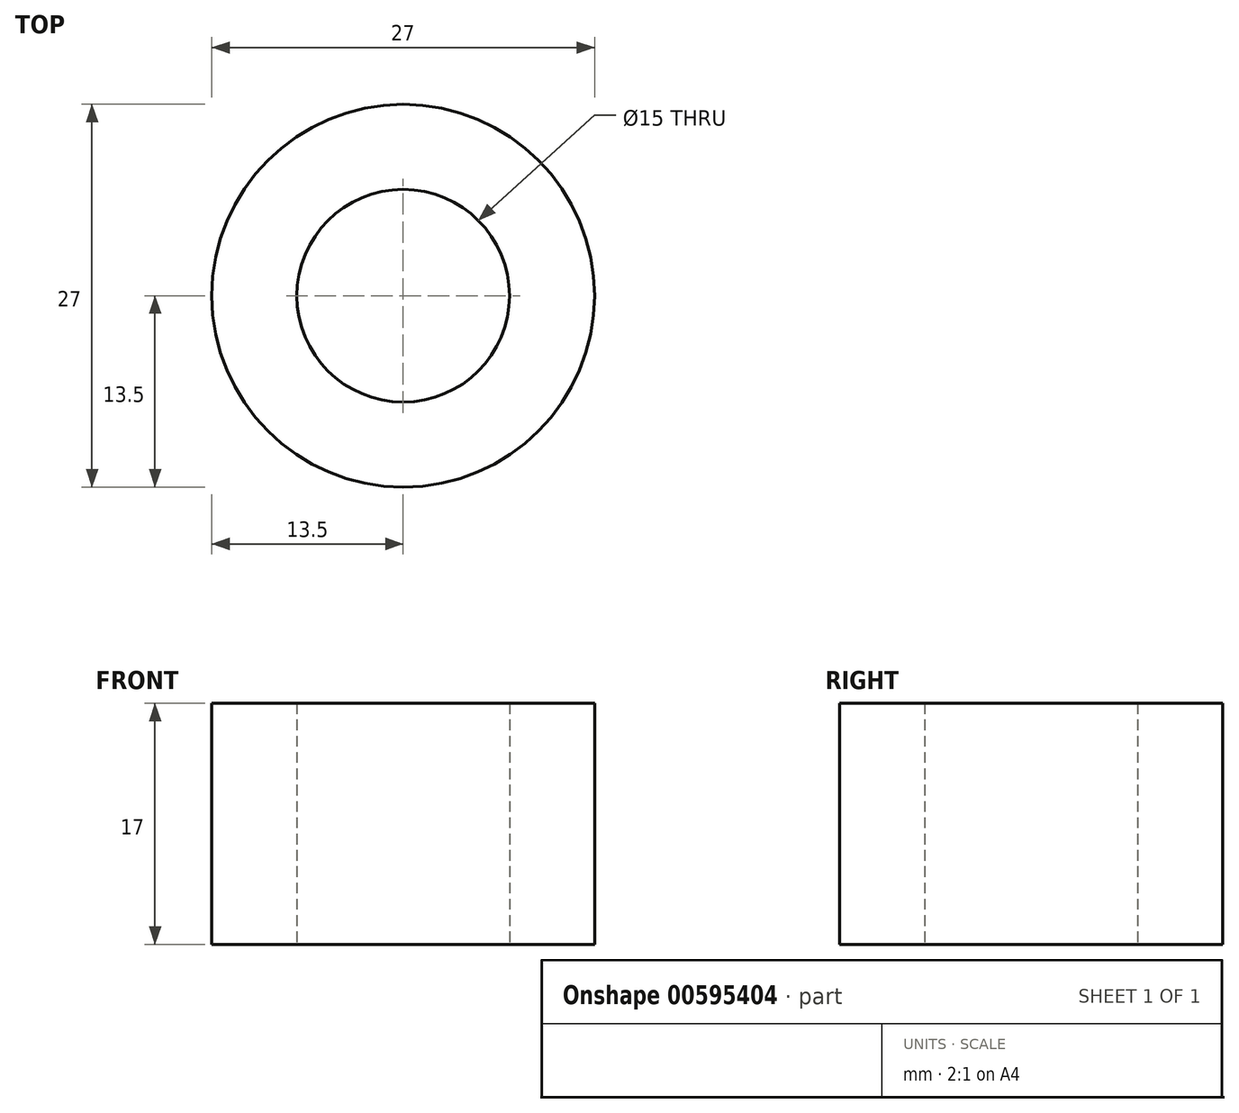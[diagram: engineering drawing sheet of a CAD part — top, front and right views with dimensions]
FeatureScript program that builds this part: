
annotation { "Feature Type Name" : "Feature", "Feature Type Description" : "" }
export const myFeature = defineFeature(function(context is Context, id is Id, definition is map)
    precondition{}
    {
        {
            var Q0;
            Q0=qCreatedBy(makeId("Top.planeOp"),FACE);
            var sketch = newSketch(context, id + "F0", { "sketchPlane" : qUnion([Q0])});
            skCircle(sketch, "E0", {"center": v(0, 0) * mm, "radius": 7.5 * mm});
            skCircle(sketch, "E1", {"center": v(0, 0) * mm, "radius": 13.5 * mm});
            skSolve(sketch);
        }
        {
            var Q0;
            Q0=makeQuery(id+"F0.imprint","IMPRINT",FACE,{"disambiguationData":[TD([[makeQuery(id+"F0.imprint","IMPRINT",EDGE,{"derivedFrom":sQuery(id+"F0.wireOp",EDGE,"E0")}),-1.0]])]});
            extrude(context, id + "F1", {"entities" : qUnion([Q0]), "depth" : 17 * mm, "offsetDistance" : 25 * mm});
        }
    });
